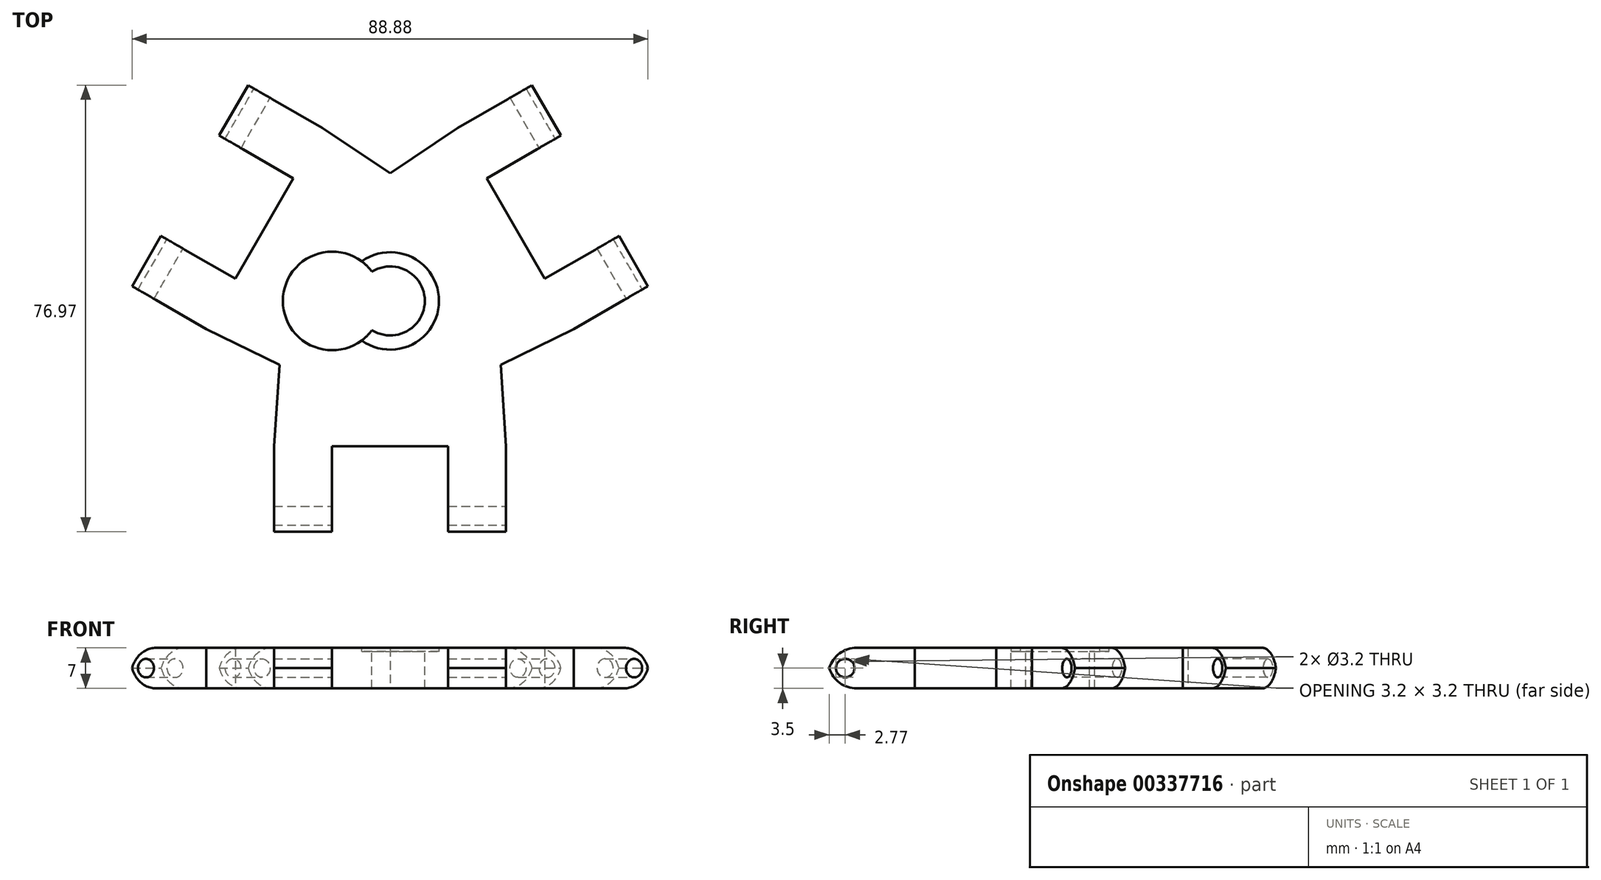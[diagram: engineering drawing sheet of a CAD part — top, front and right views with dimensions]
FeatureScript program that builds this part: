
annotation { "Feature Type Name" : "Feature", "Feature Type Description" : "" }
export const myFeature = defineFeature(function(context is Context, id is Id, definition is map)
    precondition{}
    {
        {
            var Q0;
            Q0=qCreatedBy(makeId("Top.planeOp"),FACE);
            var sketch = newSketch(context, id + "F0", { "sketchPlane" : qUnion([Q0])});
            skLineSegment(sketch, "E0", {"start": v(-0.04, -0.02) * mm, "end": v(-21.7, 12.48) * mm});
            skLineSegment(sketch, "E1", {"start": v(-21.7, 12.48) * mm, "end": v(-11.7, 29.8) * mm});
            skLineSegment(sketch, "E2", {"start": v(-21.7, 12.48) * mm, "end": v(-31.7, -4.84) * mm});
            skLineSegment(sketch, "E3", {"start": v(-0.04, -0.02) * mm, "end": v(21.6, 12.48) * mm});
            skLineSegment(sketch, "E4", {"start": v(-0.04, -0.02) * mm, "end": v(-0.04, -25.02) * mm});
            skLineSegment(sketch, "E5", {"start": v(-0.04, -25.02) * mm, "end": v(-20.04, -25.02) * mm});
            skLineSegment(sketch, "E6", {"start": v(-0.04, -25.02) * mm, "end": v(19.96, -25.02) * mm});
            skLineSegment(sketch, "E7", {"start": v(21.6, 12.48) * mm, "end": v(31.6, -4.84) * mm});
            skLineSegment(sketch, "E8", {"start": v(21.6, 12.48) * mm, "end": v(11.6, 29.8) * mm});
            skLineSegment(sketch, "E9.bottom", {"start": v(-31.7, -4.84) * mm, "end": v(-26.7, 3.82) * mm});
            skLineSegment(sketch, "E9.top", {"start": v(-44.68, 2.66) * mm, "end": v(-39.68, 11.32) * mm});
            skLineSegment(sketch, "E9.left", {"start": v(-31.7, -4.84) * mm, "end": v(-44.68, 2.66) * mm});
            skLineSegment(sketch, "E9.right", {"start": v(-26.7, 3.82) * mm, "end": v(-39.68, 11.32) * mm});
            skLineSegment(sketch, "E10.bottom", {"start": v(-11.7, 29.8) * mm, "end": v(-16.7, 21.14) * mm});
            skLineSegment(sketch, "E10.top", {"start": v(-24.68, 37.3) * mm, "end": v(-29.68, 28.64) * mm});
            skLineSegment(sketch, "E10.left", {"start": v(-11.7, 29.8) * mm, "end": v(-24.68, 37.3) * mm});
            skLineSegment(sketch, "E10.right", {"start": v(-16.7, 21.14) * mm, "end": v(-29.68, 28.64) * mm});
            skLineSegment(sketch, "E11", {"start": v(-20.04, -25.02) * mm, "end": v(-20.04, -40.02) * mm});
            skLineSegment(sketch, "E12", {"start": v(-20.04, -40.02) * mm, "end": v(-10.04, -40.02) * mm});
            skLineSegment(sketch, "E13", {"start": v(-10.04, -40.02) * mm, "end": v(-10.04, -25.02) * mm});
            skLineSegment(sketch, "E14", {"start": v(19.96, -25.02) * mm, "end": v(19.96, -40.02) * mm});
            skLineSegment(sketch, "E15", {"start": v(19.96, -40.02) * mm, "end": v(9.96, -40.02) * mm});
            skLineSegment(sketch, "E16", {"start": v(9.96, -40.02) * mm, "end": v(9.96, -25.02) * mm});
            skLineSegment(sketch, "E17", {"start": v(31.6, -4.84) * mm, "end": v(44.6, 2.66) * mm});
            skLineSegment(sketch, "E18", {"start": v(44.6, 2.66) * mm, "end": v(39.6, 11.32) * mm});
            skLineSegment(sketch, "E19", {"start": v(39.6, 11.32) * mm, "end": v(26.6, 3.82) * mm});
            skLineSegment(sketch, "E20", {"start": v(11.6, 29.8) * mm, "end": v(24.6, 37.3) * mm});
            skLineSegment(sketch, "E21", {"start": v(24.6, 37.3) * mm, "end": v(29.6, 28.64) * mm});
            skLineSegment(sketch, "E22", {"start": v(29.6, 28.64) * mm, "end": v(16.6, 21.14) * mm});
            skLineSegment(sketch, "E23", {"start": v(-0.04, -0.02) * mm, "end": v(-19.1, -11.02) * mm});
            skLineSegment(sketch, "E24", {"start": v(-0.04, -0.02) * mm, "end": v(-0.04, 21.98) * mm});
            skLineSegment(sketch, "E25", {"start": v(-0.04, -0.02) * mm, "end": v(19.01, -11.02) * mm});
            skLineSegment(sketch, "E26", {"start": v(19.01, -11.02) * mm, "end": v(31.6, -4.84) * mm});
            skLineSegment(sketch, "E27", {"start": v(19.96, -25.02) * mm, "end": v(19.01, -11.02) * mm});
            skLineSegment(sketch, "E28", {"start": v(-20.04, -25.02) * mm, "end": v(-19.1, -11.02) * mm});
            skLineSegment(sketch, "E29", {"start": v(-31.7, -4.84) * mm, "end": v(-19.1, -11.02) * mm});
            skLineSegment(sketch, "E30", {"start": v(-11.7, 29.8) * mm, "end": v(-0.04, 21.98) * mm});
            skLineSegment(sketch, "E31", {"start": v(11.6, 29.8) * mm, "end": v(-0.04, 21.98) * mm});
            skSolve(sketch);
        }
        {
            var Q0;
            Q0=qSketchRegion(id+"F0",true);
            extrude(context, id + "F1", {"entities" : qUnion([Q0]), "depth" : 7 * mm});
        }
        {
            var Q0;
            Q0=makeQuery(id+"F1.opExtrude","SWEPT_FACE",FACE,{"disambiguationData":[OSD([sQuery(id+"F0.wireOp",EDGE,"E14")])]});
            var sketch = newSketch(context, id + "F2", { "sketchPlane" : qUnion([Q0])});
            skLineSegment(sketch, "E32", {"start": v(-40.02, 3.5) * mm, "end": v(-37.02, 3.5) * mm});
            skCircle(sketch, "E33", {"center": v(-37.02, 3.5) * mm, "radius": 1.6 * mm});
            skSolve(sketch);
        }
        {
            var Q0;
            {var subQ0=sQuery(id+"F2.wireOp",EDGE,"hwxsNGN8-YZ7C-MMK4-pKxF-B9U5Xw8N2g3O");var subQ1=sQuery(id+"F2.wireOp",EDGE,"aEPsG9ev-R9g6-eiI9-y869-0mmje5FJimsM");var subQ2=makeQuery(id+"F2.imprint","INTERSECT",VERTEX,{"disambiguationData":[OD(0.0)],"derivedFrom":[subQ1,subQ0]});Q0=makeQuery(id+"F2.imprint","IMPRINT",FACE,{"disambiguationData":[TD([[makeQuery(id+"F2.imprint","IMPRINT",EDGE,{"disambiguationData":[TD([[subQ2,-1.0]])],"derivedFrom":subQ1}),1.0]])]});}
            var Q1;
            Q1=makeQuery(id+"F2.imprint","IMPRINT",FACE,{"disambiguationData":[TD([[makeQuery(id+"F2.imprint","IMPRINT",EDGE,{"derivedFrom":sQuery(id+"F2.wireOp",EDGE,"E33")}),1.0]])]});
            extrude(context, id + "F3", {"entities" : qUnion([Q0, Q1]), "operationType" : NewBodyOperationType.REMOVE, "oppositeDirection" : true, "depth" : 60 * mm});
        }
        {
            var Q0;
            Q0=makeQuery(id+"F1.opExtrude","SWEPT_FACE",FACE,{"disambiguationData":[OSD([sQuery(id+"F0.wireOp",EDGE,"E17")])]});
            var sketch = newSketch(context, id + "F4", { "sketchPlane" : qUnion([Q0])});
            skLineSegment(sketch, "E34", {"start": v(39.95, 3.5) * mm, "end": v(36.95, 3.5) * mm});
            skCircle(sketch, "E35", {"center": v(36.95, 3.5) * mm, "radius": 1.6 * mm});
            skSolve(sketch);
        }
        {
            var Q0;
            Q0=qSketchRegion(id+"F4",true);
            extrude(context, id + "F5", {"entities" : qUnion([Q0]), "operationType" : NewBodyOperationType.REMOVE, "oppositeDirection" : true, "depth" : 60 * mm});
        }
        {
            var Q0;
            Q0=makeQuery(id+"F1.opExtrude","SWEPT_FACE",FACE,{"disambiguationData":[OSD([sQuery(id+"F0.wireOp",EDGE,"E10.left")])]});
            var sketch = newSketch(context, id + "F6", { "sketchPlane" : qUnion([Q0])});
            skLineSegment(sketch, "E36", {"start": v(40.03, 3.5) * mm, "end": v(37.03, 3.5) * mm});
            skCircle(sketch, "E37", {"center": v(37.03, 3.5) * mm, "radius": 1.6 * mm});
            skSolve(sketch);
        }
        {
            var Q0;
            Q0=makeQuery(id+"F6.imprint","IMPRINT",FACE,{"disambiguationData":[TD([[makeQuery(id+"F6.imprint","IMPRINT",EDGE,{"derivedFrom":sQuery(id+"F6.wireOp",EDGE,"E37")}),1.0]])]});
            extrude(context, id + "F7", {"entities" : qUnion([Q0]), "operationType" : NewBodyOperationType.REMOVE, "oppositeDirection" : true, "depth" : 60 * mm});
        }
        {
            var Q0;
            Q0=makeQuery(id+"F1.opExtrude","CAP_EDGE",EDGE,{"disambiguationData":[OSD([sQuery(id+"F0.wireOp",EDGE,"E12")])],"isStart":false});
            var Q1;
            Q1=makeQuery(id+"F1.opExtrude","CAP_EDGE",EDGE,{"disambiguationData":[OSD([sQuery(id+"F0.wireOp",EDGE,"E12")])],"isStart":true});
            var Q2;
            Q2=makeQuery(id+"F1.opExtrude","CAP_EDGE",EDGE,{"disambiguationData":[OSD([sQuery(id+"F0.wireOp",EDGE,"E15")])],"isStart":true});
            var Q3;
            Q3=makeQuery(id+"F1.opExtrude","CAP_EDGE",EDGE,{"disambiguationData":[OSD([sQuery(id+"F0.wireOp",EDGE,"E15")])],"isStart":false});
            var Q4;
            Q4=makeQuery(id+"F1.opExtrude","CAP_EDGE",EDGE,{"disambiguationData":[OSD([sQuery(id+"F0.wireOp",EDGE,"E18")])],"isStart":false});
            var Q5;
            Q5=makeQuery(id+"F1.opExtrude","CAP_EDGE",EDGE,{"disambiguationData":[OSD([sQuery(id+"F0.wireOp",EDGE,"E18")])],"isStart":true});
            var Q6;
            Q6=makeQuery(id+"F1.opExtrude","CAP_EDGE",EDGE,{"disambiguationData":[OSD([sQuery(id+"F0.wireOp",EDGE,"E21")])],"isStart":false});
            var Q7;
            Q7=makeQuery(id+"F1.opExtrude","CAP_EDGE",EDGE,{"disambiguationData":[OSD([sQuery(id+"F0.wireOp",EDGE,"E21")])],"isStart":true});
            var Q8;
            Q8=makeQuery(id+"F1.opExtrude","CAP_EDGE",EDGE,{"disambiguationData":[OSD([sQuery(id+"F0.wireOp",EDGE,"E10.top")])],"isStart":false});
            var Q9;
            Q9=makeQuery(id+"F1.opExtrude","CAP_EDGE",EDGE,{"disambiguationData":[OSD([sQuery(id+"F0.wireOp",EDGE,"E10.top")])],"isStart":true});
            var Q10;
            Q10=makeQuery(id+"F1.opExtrude","CAP_EDGE",EDGE,{"disambiguationData":[OSD([sQuery(id+"F0.wireOp",EDGE,"E9.top")])],"isStart":false});
            var Q11;
            Q11=makeQuery(id+"F1.opExtrude","CAP_EDGE",EDGE,{"disambiguationData":[OSD([sQuery(id+"F0.wireOp",EDGE,"E9.top")])],"isStart":true});
            fillet(context, id + "F8", {"entities" : qUnion([Q0, Q1, Q2, Q3, Q4, Q5, Q6, Q7, Q8, Q9, Q10, Q11]), "radius" : 5 * mm, "tangentPropagation" : true, "allowEdgeOverflow" : false});
        }
        {
            var Q0;
            Q0=makeQuery(id+"F1.opExtrude","CAP_FACE",FACE,{"disambiguationData":[OSD([sQuery(id+"F0.wireOp",EDGE,"E1"),sQuery(id+"F0.wireOp",EDGE,"E2"),sQuery(id+"F0.wireOp",EDGE,"E5"),sQuery(id+"F0.wireOp",EDGE,"E6"),sQuery(id+"F0.wireOp",EDGE,"E7"),sQuery(id+"F0.wireOp",EDGE,"E8"),sQuery(id+"F0.wireOp",EDGE,"E9.top"),sQuery(id+"F0.wireOp",EDGE,"E9.left"),sQuery(id+"F0.wireOp",EDGE,"E9.right"),sQuery(id+"F0.wireOp",EDGE,"E10.top"),sQuery(id+"F0.wireOp",EDGE,"E10.left"),sQuery(id+"F0.wireOp",EDGE,"E10.right"),sQuery(id+"F0.wireOp",EDGE,"E11"),sQuery(id+"F0.wireOp",EDGE,"E12"),sQuery(id+"F0.wireOp",EDGE,"E13"),sQuery(id+"F0.wireOp",EDGE,"E14"),sQuery(id+"F0.wireOp",EDGE,"E15"),sQuery(id+"F0.wireOp",EDGE,"E16"),sQuery(id+"F0.wireOp",EDGE,"E17"),sQuery(id+"F0.wireOp",EDGE,"E18"),sQuery(id+"F0.wireOp",EDGE,"E19"),sQuery(id+"F0.wireOp",EDGE,"E20"),sQuery(id+"F0.wireOp",EDGE,"E21"),sQuery(id+"F0.wireOp",EDGE,"E22"),sQuery(id+"F0.wireOp",EDGE,"E26"),sQuery(id+"F0.wireOp",EDGE,"E27"),sQuery(id+"F0.wireOp",EDGE,"E28"),sQuery(id+"F0.wireOp",EDGE,"E29"),sQuery(id+"F0.wireOp",EDGE,"E30"),sQuery(id+"F0.wireOp",EDGE,"E31")])],"isStart":false});
            var sketch = newSketch(context, id + "F9", { "sketchPlane" : qUnion([Q0])});
            skSolve(sketch);
        }
        {
            var Q0;
            {var subQ9=sQuery(id+"F0.wireOp",EDGE,"E26");Q0=makeQuery(id+"F9.imprint","IMPRINT",FACE,{"disambiguationData":[TD([[makeQuery(id+"F9.imprint","IMPRINT",EDGE,{"derivedFrom":makeQuery(id+"F1.opExtrude","CAP_EDGE",EDGE,{"disambiguationData":[OSD([subQ9])],"isStart":false})}),1.0]])]});}
            var sketch = newSketch(context, id + "F10", { "sketchPlane" : qUnion([Q0])});
            skLineSegment(sketch, "E38", {"start": v(0, 0) * mm, "end": v(-10, 0) * mm});
            skCircle(sketch, "E39", {"center": v(0, 0) * mm, "radius": 5.95 * mm});
            skCircle(sketch, "E40", {"center": v(-10, 0) * mm, "radius": 8.5 * mm});
            skSolve(sketch);
        }
        {
            var Q0;
            Q0 = qSketchRegion(id + "F10", true);
            extrude(context, id + "F11", {"entities" : qUnion([Q0]), "operationType" : NewBodyOperationType.REMOVE, "oppositeDirection" : true, "depth" : 25 * mm});
        }
        {
            var Q0;
            {var subQ9=sQuery(id+"F0.wireOp",EDGE,"E26");Q0=makeQuery(id+"F9.imprint","IMPRINT",FACE,{"disambiguationData":[TD([[makeQuery(id+"F9.imprint","IMPRINT",EDGE,{"derivedFrom":makeQuery(id+"F1.opExtrude","CAP_EDGE",EDGE,{"disambiguationData":[OSD([subQ9])],"isStart":false})}),1.0]])]});}
            var sketch = newSketch(context, id + "F12", { "sketchPlane" : qUnion([Q0])});
            skCircle(sketch, "E41", {"center": v(0, 0) * mm, "radius": 8.4 * mm});
            skSolve(sketch);
        }
        {
            var Q0;
            Q0 = qSketchRegion(id + "F12", true);
            extrude(context, id + "F13", {"entities" : qUnion([Q0]), "operationType" : NewBodyOperationType.REMOVE, "oppositeDirection" : true, "depth" : .6 * mm});
        }
    });
